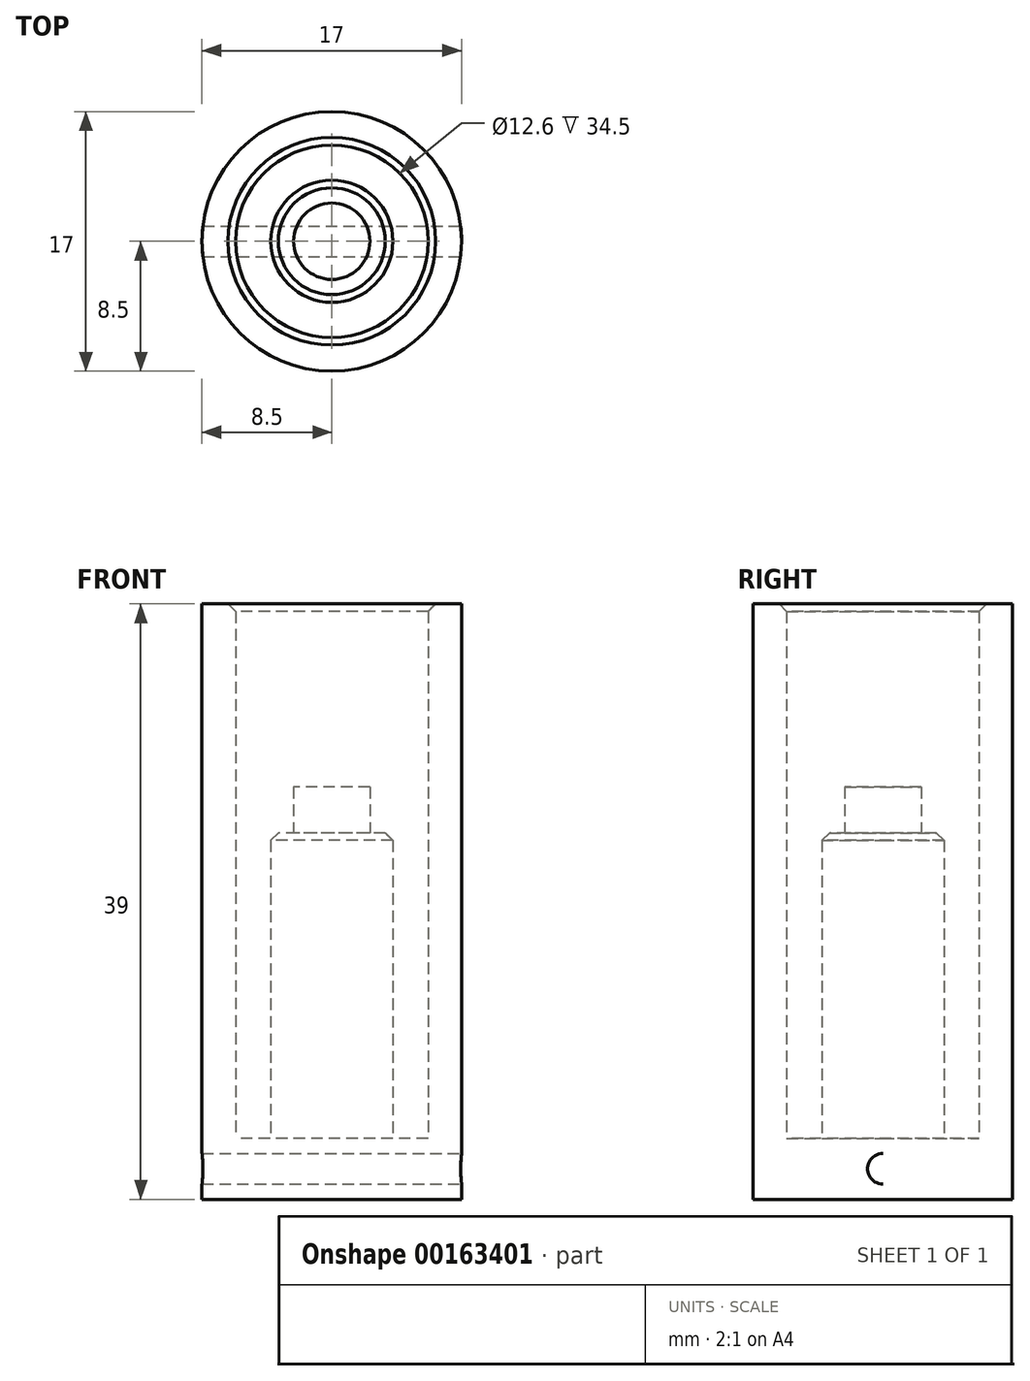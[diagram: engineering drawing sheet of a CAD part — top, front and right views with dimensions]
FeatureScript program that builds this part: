
annotation { "Feature Type Name" : "Feature", "Feature Type Description" : "" }
export const myFeature = defineFeature(function(context is Context, id is Id, definition is map)
    precondition{}
    {
        {
            var Q0;
            Q0=qCreatedBy(makeId("Top.planeOp"),FACE);
            var sketch = newSketch(context, id + "F0", { "sketchPlane" : qUnion([Q0])});
            skCircle(sketch, "E0", {"center": v(0, 0) * mm, "radius": 8.5 * mm});
            skSolve(sketch);
        }
        {
            var Q0;
            Q0=makeQuery(id+"F0.imprint","IMPRINT",FACE,{"disambiguationData":[TD([[makeQuery(id+"F0.imprint","IMPRINT",EDGE,{"derivedFrom":sQuery(id+"F0.wireOp",EDGE,"E0")}),1.0]])]});
            extrude(context, id + "F1", {"entities" : qUnion([Q0]), "endBound" : BoundingType.SYMMETRIC, "depth" : 4 * mm});
        }
        {
            var Q0;
            Q0=makeQuery(id+"F1.opExtrude","CAP_FACE",FACE,{"disambiguationData":[OSD([sQuery(id+"F0.wireOp",EDGE,"E0")])],"isStart":false});
            var sketch = newSketch(context, id + "F2", { "sketchPlane" : qUnion([Q0])});
            skCircle(sketch, "E1", {"center": v(0, 0) * mm, "radius": 4 * mm});
            skSolve(sketch);
        }
        {
            var Q0;
            Q0=makeQuery(id+"F2.imprint","IMPRINT",FACE,{"disambiguationData":[TD([[makeQuery(id+"F2.imprint","IMPRINT",EDGE,{"derivedFrom":sQuery(id+"F2.wireOp",EDGE,"E1")}),1.0]])]});
            var Q1;
            Q1=sQuery(id+"F2.wireOp",EDGE,"E1");
            extrude(context, id + "F3", {"entities" : qUnion([Q0]), "operationType" : NewBodyOperationType.ADD, "surfaceEntities" : qUnion([Q1]), "depth" : 20 * mm});
        }
        {
            var Q0;
            Q0=makeQuery(id+"F1.opExtrude","CAP_FACE",FACE,{"disambiguationData":[OSD([sQuery(id+"F0.wireOp",EDGE,"E0")])],"isStart":false});
            var sketch = newSketch(context, id + "F4", { "sketchPlane" : qUnion([Q0])});
            skCircle(sketch, "E2", {"center": v(0, 0) * mm, "radius": 6.3 * mm});
            skCircle(sketch, "E3", {"center": v(0, 0) * mm, "radius": 8.5 * mm});
            skSolve(sketch);
        }
        {
            var Q0;
            Q0=makeQuery(id+"F4.imprint","IMPRINT",FACE,{"disambiguationData":[TD([[makeQuery(id+"F4.imprint","IMPRINT",EDGE,{"derivedFrom":sQuery(id+"F4.wireOp",EDGE,"E2")}),-1.0]])]});
            extrude(context, id + "F5", {"entities" : qUnion([Q0]), "operationType" : NewBodyOperationType.ADD, "depth" : 35 * mm});
        }
        {
            var Q0;
            Q0=makeQuery(id+"F3.opExtrude","CAP_EDGE",EDGE,{"disambiguationData":[OSD([sQuery(id+"F2.wireOp",EDGE,"E1")])],"isStart":false});
            chamfer(context, id + "F6", {"entities" : qUnion([Q0]), "width" : 0.5 * mm, "tangentPropagation" : true});
        }
        {
            var Q0;
            Q0=makeQuery(id+"F5.opExtrude","CAP_EDGE",EDGE,{"disambiguationData":[OSD([sQuery(id+"F4.wireOp",EDGE,"E2")])],"isStart":false});
            chamfer(context, id + "F7", {"entities" : qUnion([Q0]), "width" : 0.5 * mm, "tangentPropagation" : true});
        }
        {
            var Q0;
            Q0=qCreatedBy(makeId("Top.planeOp"),FACE);
            var sketch = newSketch(context, id + "F8", { "sketchPlane" : qUnion([Q0])});
            skCircle(sketch, "E4", {"center": v(0, 0) * mm, "radius": 2.5 * mm});
            skSolve(sketch);
        }
        {
            var Q0;
            Q0 = qSketchRegion(id + "F8", true);
            var Q1;
            Q1=sQuery(id+"F8.wireOp",EDGE,"E4");
            extrude(context, id + "F9", {"entities" : qUnion([Q0]), "operationType" : NewBodyOperationType.ADD, "surfaceEntities" : qUnion([Q1]), "depth" : 25 * mm});
        }
        {
            var Q0;
            Q0=qCreatedBy(makeId("Right.planeOp"),FACE);
            var sketch = newSketch(context, id + "F10", { "sketchPlane" : qUnion([Q0])});
            skCircle(sketch, "E5", {"center": v(0, 0) * mm, "radius": 1 * mm});
            skSolve(sketch);
        }
        {
            var Q0;
            Q0 = qSketchRegion(id + "F10", true);
            var Q1;
            Q1=sQuery(id+"F10.wireOp",EDGE,"E5");
            extrude(context, id + "F11", {"entities" : qUnion([Q0]), "operationType" : NewBodyOperationType.REMOVE, "surfaceEntities" : qUnion([Q1]), "endBound" : BoundingType.SYMMETRIC, "oppositeDirection" : true, "depth" : 25 * mm});
        }
    });
